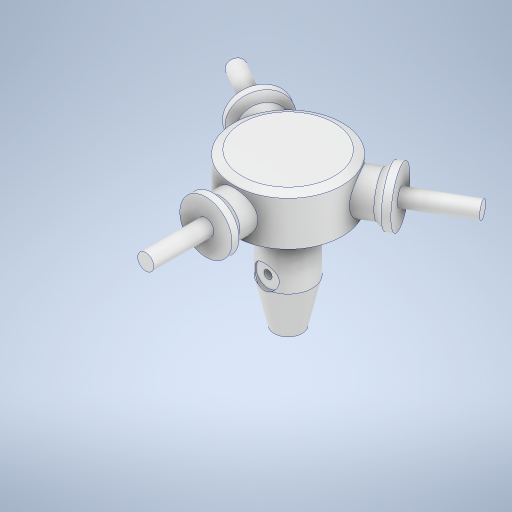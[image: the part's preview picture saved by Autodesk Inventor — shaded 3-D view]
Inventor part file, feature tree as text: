
AUTODESK INVENTOR PART (.ipt)
format: ipt  version: 2023.2 (Build 272271000, 271)  size: 370,688 bytes
history: native  units: mm
features: extrude x8, sketch x8, chamfer x5, plane x2, mirror x1, pattern_circular x1
ambient origin geometry x8: Origin, YZ Plane, XZ Plane, XY Plane, X Axis, Y Axis, Z Axis, Center Point
bodies: Volumenkörper1 (feature_tree)
feature tree (25):
  extrude  "Extrusion1"  Depth=2.0mm TaperAngle=0.0deg
  chamfer  "Fase5"  Distance=2.0mm Angle=45.0deg
  chamfer  "Fase1"  Distance=25.0mm
  extrude  "Extrusion2"  Depth=2.0mm TaperAngle=45.0deg
  chamfer  "Fase2"  Distance=33.0mm
  chamfer  "Fase3"  [1 undecoded]
  extrude  "Extrusion3"  Depth=6.0mm
  extrude  "Extrusion4"  Depth=15.0mm TaperAngle=0.0deg
  plane  "Arbeitsebene1"
  extrude  "Extrusion5"  Depth=15.0mm
  mirror  "Spiegeln1"
  sketch  "Skizze6"  dims[d19=11.5mm d20=0.0mm d21=0.0mm]
  plane  "Arbeitsebene2"
  extrude  "Extrusion6"  Depth=10.0mm
  sketch  "Skizze7"  dims[d22=6.0mm d23=6.0mm]
  extrude  "Extrusion7"  Depth=15.0mm
  chamfer  "Fase4"  Distance=1.0mm
  extrude  "Extrusion8"  Depth=15.0mm TaperAngle=360.0deg
  pattern_circular  "Runde Anordnung1"  [2 undecoded]
  sketch  "Skizze1"  dims[d0=27.0mm d1=13.0mm d2=0.0mm d3=2.0mm d4=1.0mm d5=45.0deg]
  sketch  "Skizze2"  dims[d6=12.0mm d7=25.0mm d8=0.0mm]
  sketch  "Skizze3"  dims[d9=3.0mm d10=2.0mm d11=45.0deg d12=2.5mm d13=11.0mm d14=45.0deg]
  sketch  "Skizze4"  dims[d15=6.0mm d16=33.0mm d17=0.0mm]
  sketch  "Skizze5"  dims[d18=2.0mm]
  sketch  "Skizze8"  dims[d24=6.0mm d25=1.0mm d26=0.0mm d27=11.5mm d28=10.0mm d29=17.0mm d30=1.0mm d31=0.0mm d32=30.0mm d33=360.0deg d35=13.0mm d36=3.5mm d37=0.0mm d38=1.75mm d39=1.5mm d40=45.0deg d41=1.0mm d42=2.0mm d43=45.0deg d44=6.5mm d45=4.0mm d46=15.0mm d47=0.0mm]
note: 3 required parameter values undecoded (feature->parameter linkage not recoverable at this tier; creation-order binding heuristic only, values carry confidence <= 0.55)
